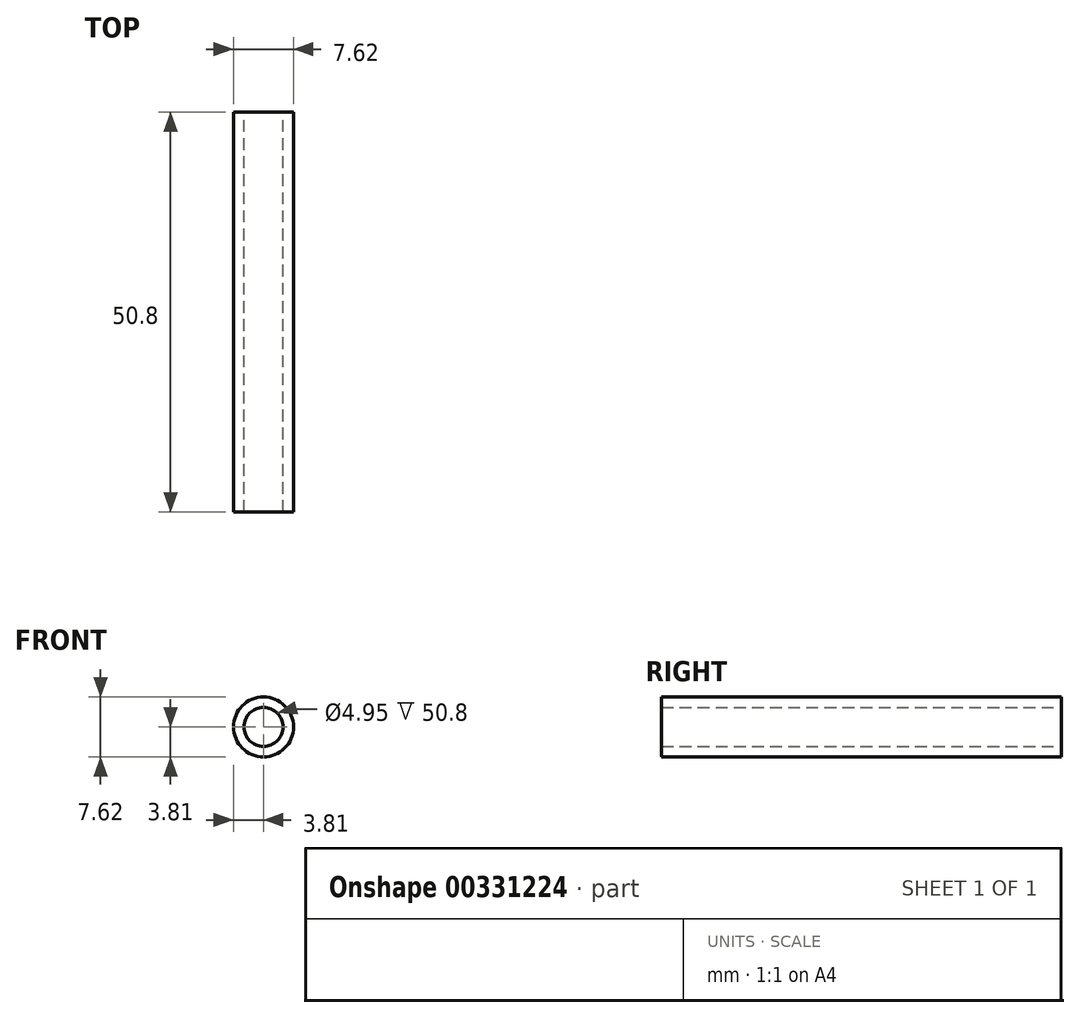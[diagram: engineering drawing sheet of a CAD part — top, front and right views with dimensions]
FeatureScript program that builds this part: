
annotation { "Feature Type Name" : "Feature", "Feature Type Description" : "" }
export const myFeature = defineFeature(function(context is Context, id is Id, definition is map)
    precondition{}
    {
        {
            var Q0;
            Q0=qCreatedBy(makeId("Front.planeOp"),FACE);
            var sketch = newSketch(context, id + "F0", { "sketchPlane" : qUnion([Q0])});
            skCircle(sketch, "E0", {"center": v(0, 0) * mm, "radius": 2.48 * mm});
            skCircle(sketch, "E1", {"center": v(0, 0) * mm, "radius": 3.81 * mm});
            skSolve(sketch);
        }
        {
            var Q0;
            Q0 = qSketchRegion(id + "F0", true);
            extrude(context, id + "F1", {"entities" : qUnion([Q0]), "depth" : 50.8 * mm});
        }
    });
